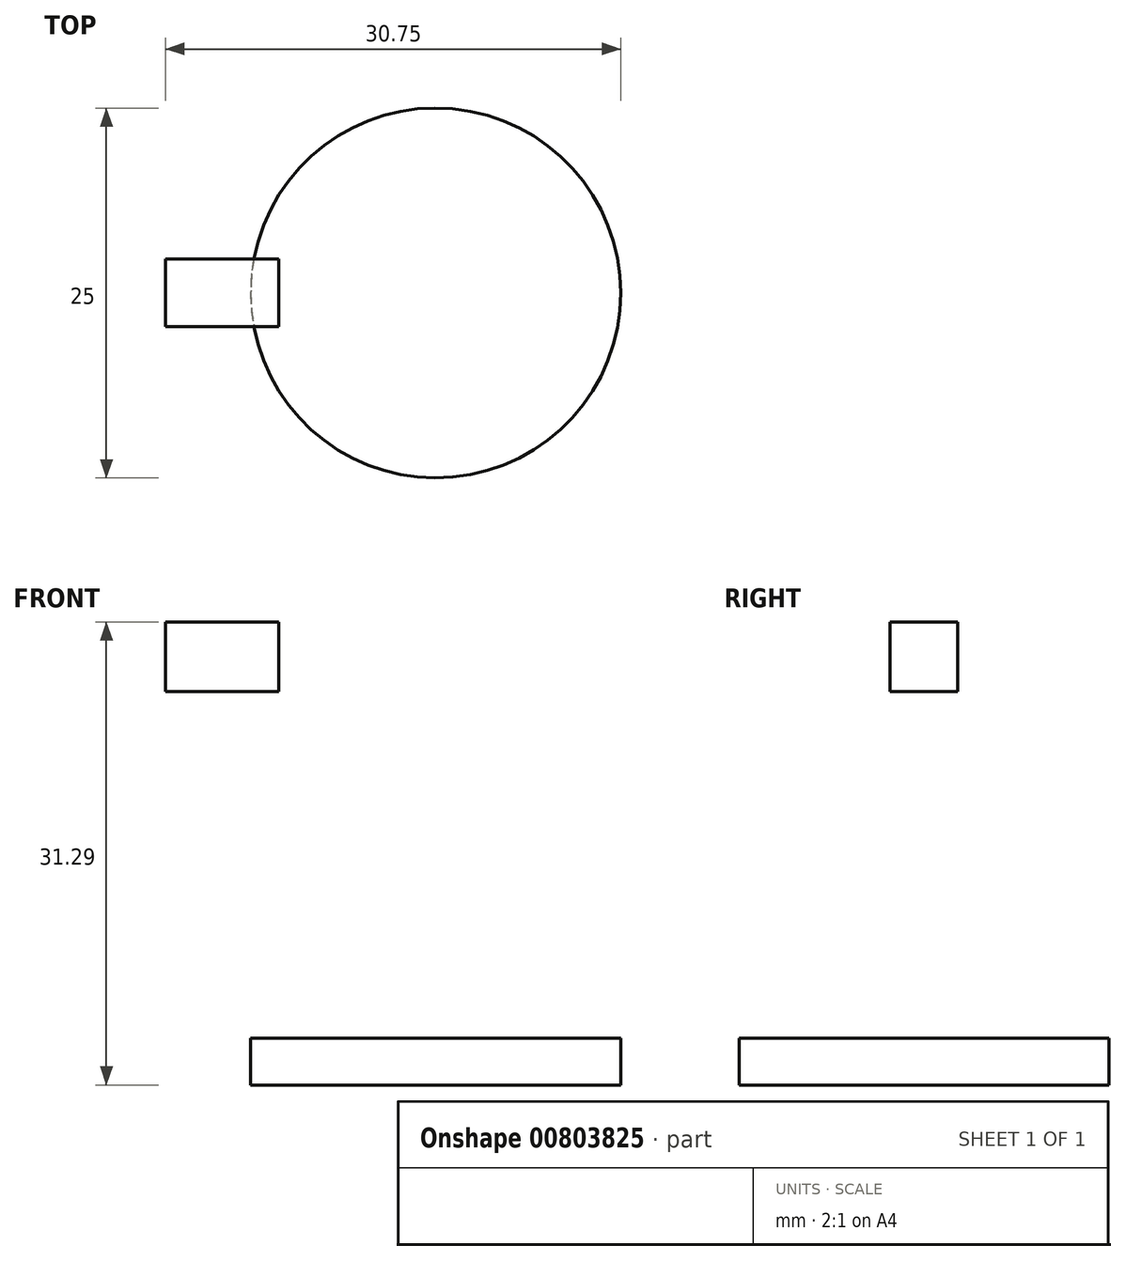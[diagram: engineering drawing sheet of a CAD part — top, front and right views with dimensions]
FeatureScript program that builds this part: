
annotation { "Feature Type Name" : "Feature", "Feature Type Description" : "" }
export const myFeature = defineFeature(function(context is Context, id is Id, definition is map)
    precondition{}
    {
        {
            var Q0;
            Q0=qCreatedBy(makeId("Top.planeOp"),FACE);
            var sketch = newSketch(context, id + "F0", { "sketchPlane" : qUnion([Q0])});
            skCircle(sketch, "E0", {"center": v(0, 0) * mm, "radius": 12.5 * mm});
            skSolve(sketch);
        }
        {
            var Q0;
            Q0=makeQuery(id+"F0.imprint","IMPRINT",FACE,{"disambiguationData":[TD([[makeQuery(id+"F0.imprint","IMPRINT",EDGE,{"derivedFrom":sQuery(id+"F0.wireOp",EDGE,"E0")}),1.0]])]});
            extrude(context, id + "F1", {"entities" : qUnion([Q0]), "depth" : 3.17 * mm, "offsetDistance" : 25.4 * mm});
        }
        {
            var Q0;
            Q0=qCreatedBy(makeId("Front.planeOp"),FACE);
            var sketch = newSketch(context, id + "F2", { "sketchPlane" : qUnion([Q0])});
            skLineSegment(sketch, "E1.bottom", {"start": v(-10.61, 3.17) * mm, "end": v(17.33, 3.17) * mm});
            skLineSegment(sketch, "E1.top", {"start": v(-10.61, 35.17) * mm, "end": v(17.33, 35.17) * mm});
            skLineSegment(sketch, "E1.left", {"start": v(-10.61, 3.18) * mm, "end": v(-10.61, 35.17) * mm});
            skLineSegment(sketch, "E1.right", {"start": v(17.33, 3.18) * mm, "end": v(17.33, 35.17) * mm});
            skLineSegment(sketch, "E2", {"start": v(-10.61, 3.17) * mm, "end": v(-10.61, 6.78) * mm});
            skLineSegment(sketch, "E3", {"start": v(-10.61, 6.78) * mm, "end": v(-4.95, 6.78) * mm});
            skLineSegment(sketch, "E4", {"start": v(-4.95, 6.78) * mm, "end": v(-3, 17.34) * mm});
            skLineSegment(sketch, "E5", {"start": v(-3, 17.34) * mm, "end": v(-3, 26.6) * mm});
            skLineSegment(sketch, "E6", {"start": v(-3, 26.6) * mm, "end": v(-18.25, 26.6) * mm});
            skLineSegment(sketch, "E7", {"start": v(-18.25, 26.6) * mm, "end": v(-18.25, 31.29) * mm});
            skLineSegment(sketch, "E8", {"start": v(-18.25, 31.29) * mm, "end": v(-4.17, 31.29) * mm});
            skLineSegment(sketch, "E9", {"start": v(-4.17, 31.29) * mm, "end": v(-4.17, 35.17) * mm});
            skLineSegment(sketch, "E10", {"start": v(-4.17, 35.17) * mm, "end": v(4.57, 35.17) * mm});
            skLineSegment(sketch, "E11", {"start": v(4.57, 35.17) * mm, "end": v(4.57, 31.42) * mm});
            skLineSegment(sketch, "E12", {"start": v(4.57, 31.42) * mm, "end": v(10.17, 30.24) * mm});
            skLineSegment(sketch, "E13", {"start": v(10.17, 30.24) * mm, "end": v(12, 27.25) * mm});
            skLineSegment(sketch, "E14", {"start": v(12, 27.25) * mm, "end": v(13.43, 24.64) * mm});
            skLineSegment(sketch, "E15", {"start": v(13.43, 24.64) * mm, "end": v(10.17, 24.64) * mm});
            skLineSegment(sketch, "E16", {"start": v(10.17, 24.64) * mm, "end": v(6.4, 27.25) * mm});
            skLineSegment(sketch, "E17", {"start": v(6.4, 27.25) * mm, "end": v(6.4, 17.47) * mm});
            skLineSegment(sketch, "E18", {"start": v(6.4, 17.47) * mm, "end": v(8.6, 10.82) * mm});
            skLineSegment(sketch, "E19", {"start": v(8.6, 10.82) * mm, "end": v(8.6, 3.17) * mm});
            skLineSegment(sketch, "E20", {"start": v(8.6, 3.17) * mm, "end": v(4.57, 3.17) * mm});
            skLineSegment(sketch, "E21", {"start": v(4.57, 3.17) * mm, "end": v(4.57, 10.43) * mm});
            skLineSegment(sketch, "E22", {"start": v(4.57, 10.43) * mm, "end": v(-0.52, 10.69) * mm});
            skLineSegment(sketch, "E23", {"start": v(-0.52, 10.69) * mm, "end": v(-0.52, 3.17) * mm});
            skLineSegment(sketch, "E24", {"start": v(-0.52, 3.17) * mm, "end": v(-10.61, 3.18) * mm});
            skSolve(sketch);
        }
        {
            var Q0;
            Q0=makeQuery(id+"F2.imprint","IMPRINT",FACE,{"disambiguationData":[TD([[makeQuery(id+"F2.imprint","IMPRINT",EDGE,{"derivedFrom":sQuery(id+"F2.wireOp",EDGE,"E2")}),-1.0]])]});
            var Q1;
            {var subQ5=sQuery(id+"F2.wireOp",EDGE,"E7");Q1=makeQuery(id+"F2.imprint","IMPRINT",FACE,{"disambiguationData":[TD([[makeQuery(id+"F2.imprint","IMPRINT",EDGE,{"derivedFrom":subQ5}),-1.0]])]});}
            extrude(context, id + "F3", {"entities" : qUnion([Q0, Q1]), "operationType" : NewBodyOperationType.ADD, "endBound" : BoundingType.SYMMETRIC, "depth" : 4.57 * mm, "offsetDistance" : 25.4 * mm});
        }
    });
